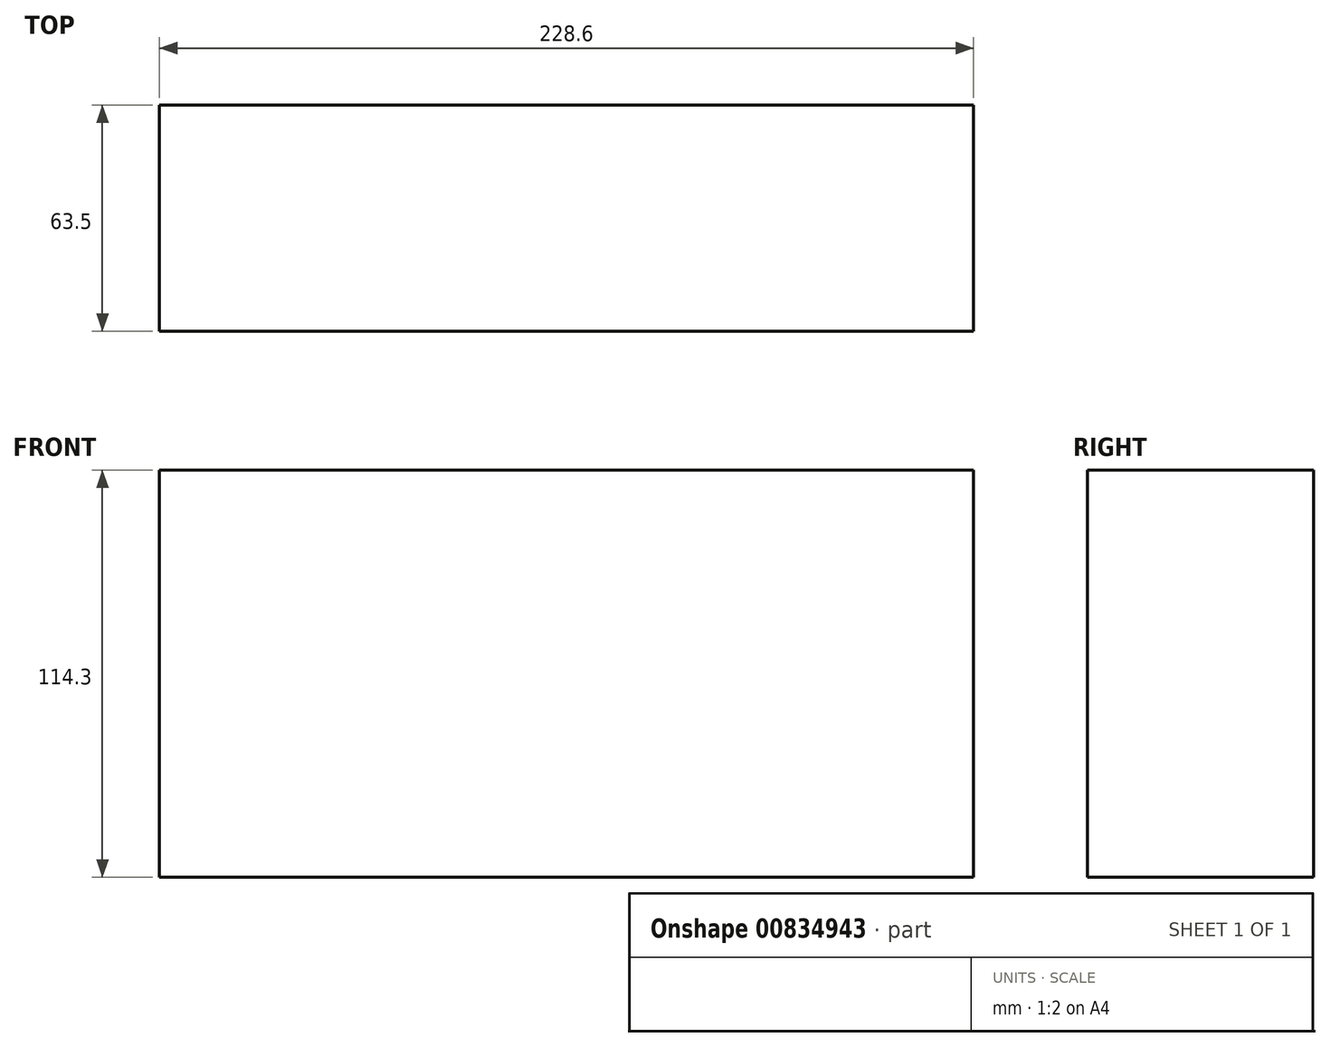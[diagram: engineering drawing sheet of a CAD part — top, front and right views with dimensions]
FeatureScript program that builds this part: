
annotation { "Feature Type Name" : "Feature", "Feature Type Description" : "" }
export const myFeature = defineFeature(function(context is Context, id is Id, definition is map)
    precondition{}
    {
        {
            var Q0;
            Q0=qCreatedBy(makeId("Top.planeOp"),FACE);
            var sketch = newSketch(context, id + "F0", { "sketchPlane" : qUnion([Q0])});
            skLineSegment(sketch, "E0.bottom", {"start": v(0, 0) * mm, "end": v(228.6, 0) * mm});
            skLineSegment(sketch, "E0.top", {"start": v(0, 63.5) * mm, "end": v(228.6, 63.5) * mm});
            skLineSegment(sketch, "E0.left", {"start": v(0, 0) * mm, "end": v(0, 63.5) * mm});
            skLineSegment(sketch, "E0.right", {"start": v(228.6, 0) * mm, "end": v(228.6, 63.5) * mm});
            skSolve(sketch);
        }
        {
            var Q0;
            Q0 = qSketchRegion(id + "F0", true);
            extrude(context, id + "F1", {"entities" : qUnion([Q0]), "depth" : 114.3 * mm, "offsetDistance" : 25.4 * mm});
        }
    });
